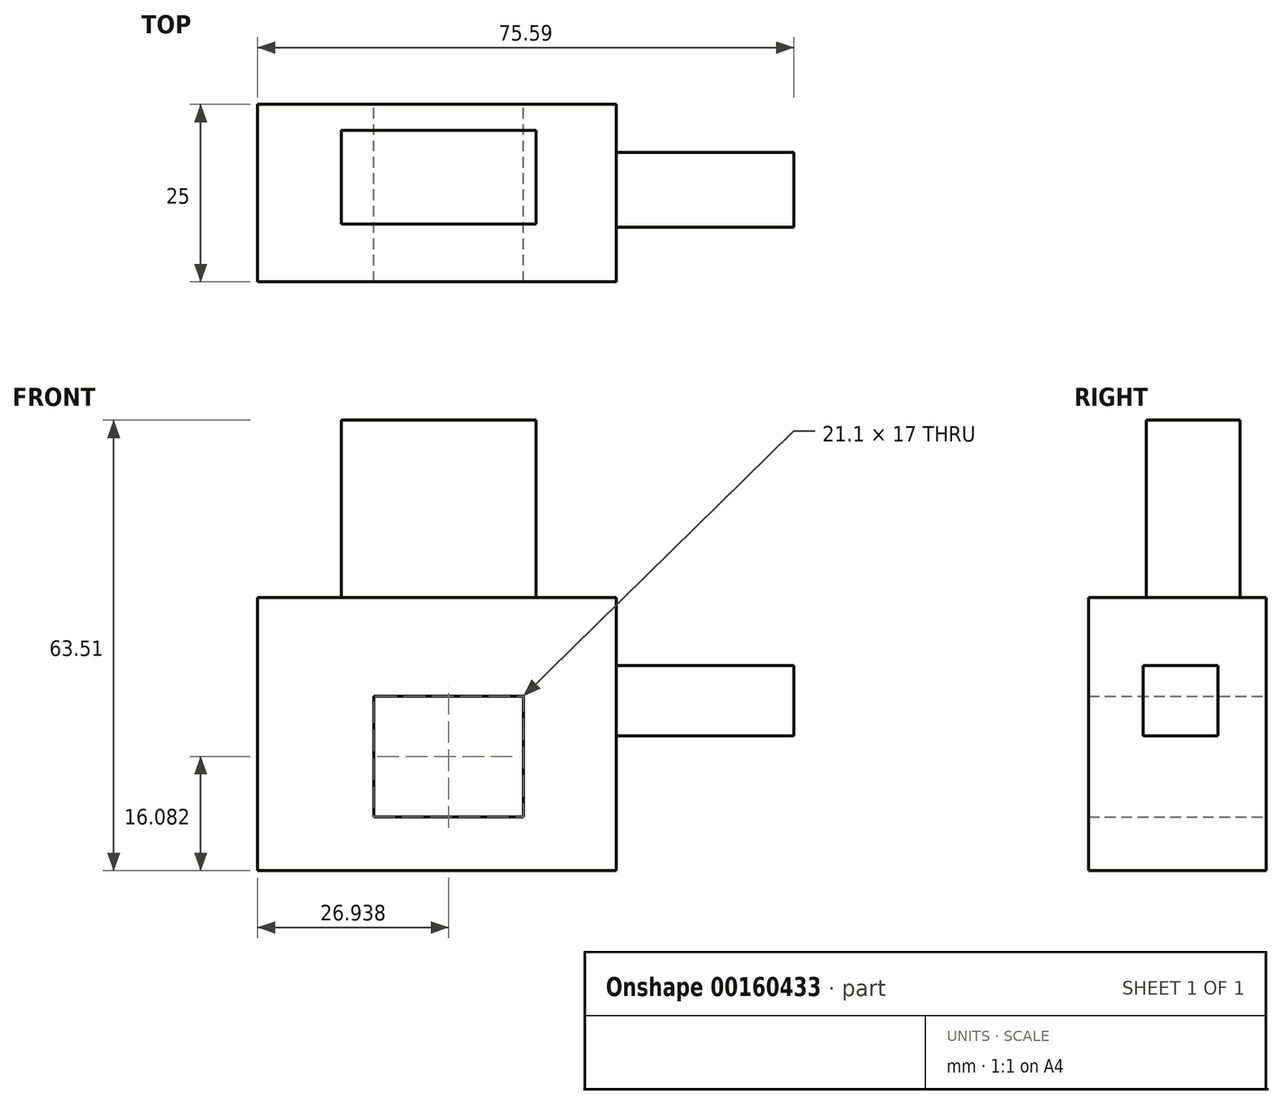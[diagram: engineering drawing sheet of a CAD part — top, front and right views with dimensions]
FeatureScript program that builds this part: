
annotation { "Feature Type Name" : "Feature", "Feature Type Description" : "" }
export const myFeature = defineFeature(function(context is Context, id is Id, definition is map)
    precondition{}
    {
        {
            var Q0;
            Q0=qCreatedBy(makeId("Front.planeOp"),FACE);
            var sketch = newSketch(context, id + "F0", { "sketchPlane" : qUnion([Q0])});
            skLineSegment(sketch, "E0.bottom", {"start": v(-27.04, 25.5) * mm, "end": v(23.55, 25.5) * mm});
            skLineSegment(sketch, "E0.top", {"start": v(-27.04, -13) * mm, "end": v(23.55, -13) * mm});
            skLineSegment(sketch, "E0.left", {"start": v(-27.04, 25.5) * mm, "end": v(-27.04, -13) * mm});
            skLineSegment(sketch, "E0.right", {"start": v(23.55, 25.5) * mm, "end": v(23.55, -13) * mm});
            skLineSegment(sketch, "E1.bottom", {"start": v(-10.65, 11.57) * mm, "end": v(10.45, 11.57) * mm});
            skLineSegment(sketch, "E1.top", {"start": v(-10.65, -5.43) * mm, "end": v(10.45, -5.43) * mm});
            skLineSegment(sketch, "E1.left", {"start": v(-10.65, 11.57) * mm, "end": v(-10.65, -5.43) * mm});
            skLineSegment(sketch, "E1.right", {"start": v(10.45, 11.57) * mm, "end": v(10.45, -5.43) * mm});
            skSolve(sketch);
        }
        {
            var Q0;
            Q0=makeQuery(id+"F0.imprint","IMPRINT",FACE,{"disambiguationData":[TD([[makeQuery(id+"F0.imprint","IMPRINT",EDGE,{"derivedFrom":sQuery(id+"F0.wireOp",EDGE,"E0.bottom")}),-1.0]])]});
            extrude(context, id + "F1", {"entities" : qUnion([Q0]), "depth" : 25 * mm});
        }
        {
            var Q0;
            Q0=makeQuery(id+"F1.opExtrude","SWEPT_FACE",FACE,{"disambiguationData":[OSD([sQuery(id+"F0.wireOp",EDGE,"E0.bottom")])]});
            var sketch = newSketch(context, id + "F2", { "sketchPlane" : qUnion([Q0])});
            skLineSegment(sketch, "E2.bottom", {"start": v(-15.2, -3.65) * mm, "end": v(12.2, -3.65) * mm});
            skLineSegment(sketch, "E2.top", {"start": v(-15.2, -16.87) * mm, "end": v(12.2, -16.87) * mm});
            skLineSegment(sketch, "E2.left", {"start": v(-15.2, -3.65) * mm, "end": v(-15.2, -16.87) * mm});
            skLineSegment(sketch, "E2.right", {"start": v(12.2, -3.65) * mm, "end": v(12.2, -16.87) * mm});
            skSolve(sketch);
        }
        {
            var Q0;
            Q0=makeQuery(id+"F2.imprint","IMPRINT",FACE,{"disambiguationData":[TD([[makeQuery(id+"F2.imprint","IMPRINT",EDGE,{"derivedFrom":sQuery(id+"F2.wireOp",EDGE,"E2.bottom")}),-1.0]])]});
            extrude(context, id + "F3", {"entities" : qUnion([Q0]), "operationType" : NewBodyOperationType.ADD, "depth" : 25 * mm});
        }
        {
            var Q0;
            Q0=makeQuery(id+"F1.opExtrude","SWEPT_FACE",FACE,{"disambiguationData":[OSD([sQuery(id+"F0.wireOp",EDGE,"E0.right")])]});
            var sketch = newSketch(context, id + "F4", { "sketchPlane" : qUnion([Q0])});
            skLineSegment(sketch, "E3.bottom", {"start": v(-17.31, 15.92) * mm, "end": v(-6.8, 15.92) * mm});
            skLineSegment(sketch, "E3.top", {"start": v(-17.31, 5.99) * mm, "end": v(-6.8, 5.99) * mm});
            skLineSegment(sketch, "E3.left", {"start": v(-17.31, 15.92) * mm, "end": v(-17.31, 5.99) * mm});
            skLineSegment(sketch, "E3.right", {"start": v(-6.8, 15.92) * mm, "end": v(-6.8, 5.99) * mm});
            skSolve(sketch);
        }
        {
            var Q0;
            Q0=makeQuery(id+"F4.imprint","IMPRINT",FACE,{"disambiguationData":[TD([[makeQuery(id+"F4.imprint","IMPRINT",EDGE,{"derivedFrom":sQuery(id+"F4.wireOp",EDGE,"E3.bottom")}),-1.0]])]});
            extrude(context, id + "F5", {"entities" : qUnion([Q0]), "operationType" : NewBodyOperationType.ADD, "depth" : 25 * mm});
        }
    });
